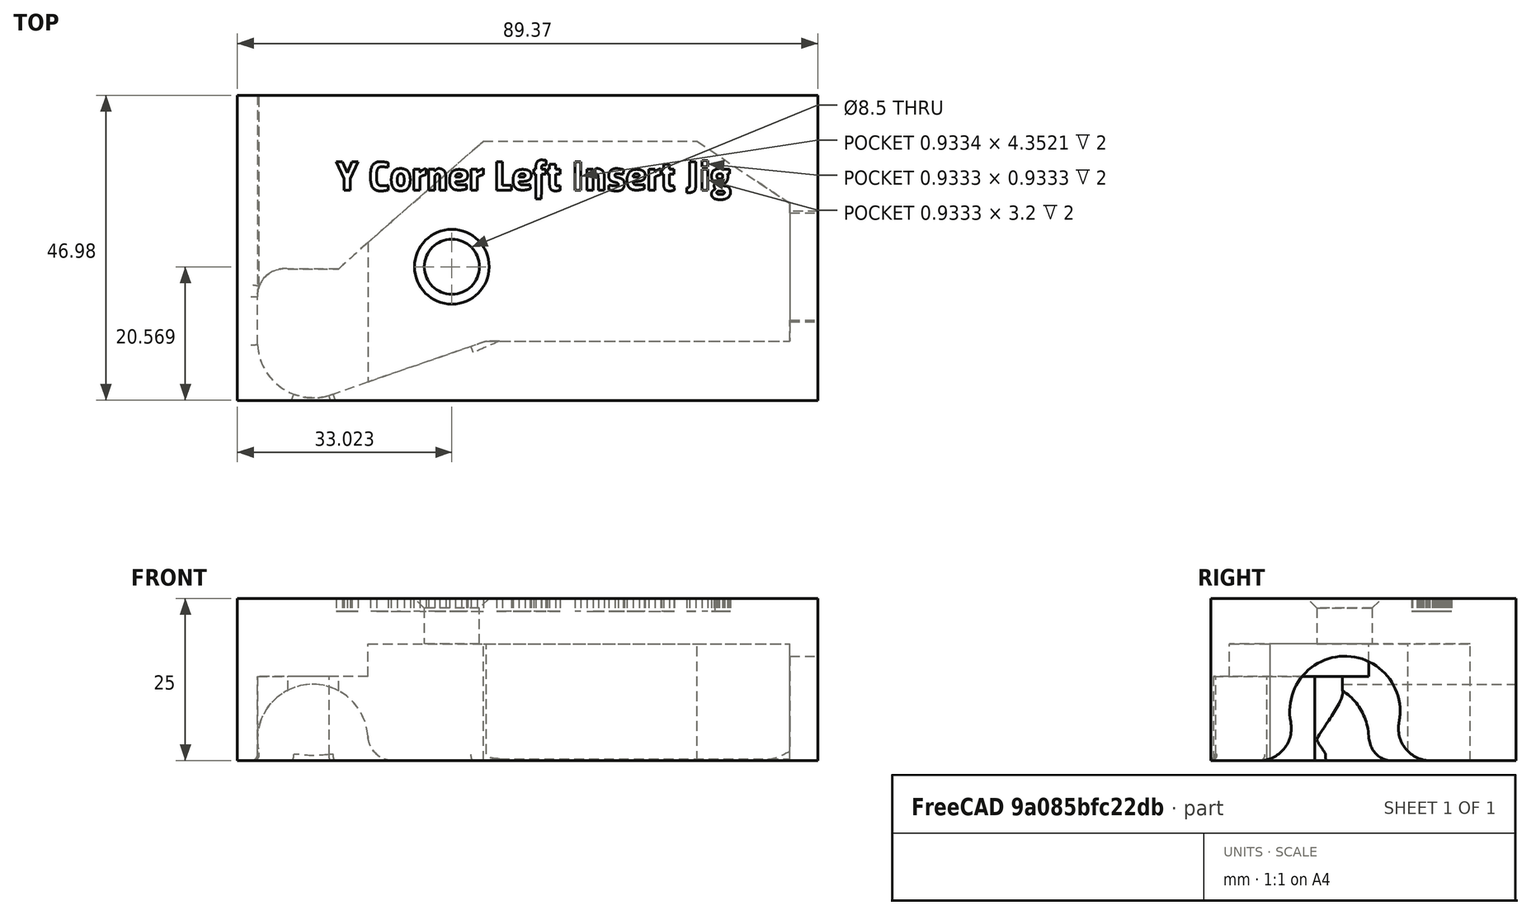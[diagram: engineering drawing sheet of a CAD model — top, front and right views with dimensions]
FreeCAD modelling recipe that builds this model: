
FCSTD DOCUMENT  (FreeCAD 0.17R9537 (Git))
Label: y_corner_left_insert_jig
License: All rights reserved
LicenseURL: http://en.wikipedia.org/wiki/All_rights_reserved
objects: Sketcher::SketchObject×8, PartDesign::Pocket×6, PartDesign::Fillet×3, Mesh::Feature×1, PartDesign::Pad×1, Part::Feature×1, PartDesign::Plane×1, PartDesign::Chamfer×1, Part::Part2DObjectPython×1, PartDesign::Body×1
note: 30 computed .brp shape members not serialized (recipe doc carries the construction recipe); baked Part::Feature solids carry a one-line shape summary decoded from their .brp

FEATURE [Mesh::Feature] y_corner_left_v2_4  label="y_corner_left_v2.4"
  Placement = pos=(-95,-15,-13) rot=(0,0,1;0rad)
FEATURE [Sketcher::SketchObject] Sketch
  MapMode = 5
  Support = -> [XY_Plane]
  sketch-geometry (4):
    g0: LineSegment StartX=-41.2454 StartY=-29.3641 StartZ=0 EndX=48.1248 EndY=-29.3641 EndZ=0
    g1: LineSegment StartX=48.1248 StartY=-29.3641 StartZ=0 EndX=48.1248 EndY=17.6233 EndZ=0
    g2: LineSegment StartX=48.1248 StartY=17.6233 StartZ=0 EndX=-41.2454 EndY=17.6233 EndZ=0
    g3: LineSegment StartX=-41.2454 StartY=17.6233 StartZ=0 EndX=-41.2454 EndY=-29.3641 EndZ=0
  constraints (8):
    c: Coincident(g0,g1)
    c: Coincident(g1,g2)
    c: Coincident(g2,g3)
    c: Coincident(g3,g0)
    c: Horizontal(g0)
    c: Horizontal(g2)
    c: Vertical(g1)
    c: Vertical(g3)
FEATURE [PartDesign::Pad] Pad
  Length = 25
  Length2 = 100
  Profile = -> Sketch
  Type = 0
FEATURE [Part::Feature] y_corner_left_v2_4001
  Placement = pos=(0,0,12) rot=(0,0,1;0rad)
  shape: bbox 81.06 x 37.98 x 18.29 mm, 18592 faces, 0 solids (baked)
FEATURE [Sketcher::SketchObject] Sketch001
  MapMode = 5
  Placement = pos=(0,0,0) rot=(1,0,0;3.14159rad)
  Support = -> [Pad]
  sketch-geometry (7):
    g0: LineSegment StartX=-21.1438 StartY=5.05934 StartZ=0 EndX=-3.38972 EndY=-10.5427 EndZ=0
    g1: LineSegment StartX=-3.38972 StartY=-10.5427 StartZ=0 EndX=29.5098 EndY=-10.5427 EndZ=0
    g2: LineSegment StartX=29.5098 StartY=-10.5427 StartZ=0 EndX=43.8429 EndY=-0.932231 EndZ=0
    g3: LineSegment StartX=43.8429 StartY=-0.932231 StartZ=0 EndX=43.8429 EndY=20.2526 EndZ=0
    g4: LineSegment StartX=-21.1438 StartY=5.05934 StartZ=0 EndX=-21.1438 EndY=26.5193 EndZ=0
    g5: LineSegment StartX=-21.1438 StartY=26.5193 StartZ=0 EndX=-2.94605 EndY=20.2526 EndZ=0
    g6: LineSegment StartX=-2.94605 StartY=20.2526 StartZ=0 EndX=43.8429 EndY=20.2526 EndZ=0
  constraints (11):
    c: Coincident(g1,g0)
    c: Horizontal(g1)
    c: Coincident(g2,g1)
    c: Coincident(g3,g2)
    c: Vertical(g3)
    c: Coincident(g4,g0)
    c: Vertical(g4)
    c: Coincident(g5,g4)
    c: Coincident(g6,g5)
    c: Coincident(g6,g3)
    c: Horizontal(g6)
FEATURE [PartDesign::Pocket] Pocket
  BaseFeature = -> Pad
  Length = 18
  Profile = -> Sketch001
  Type = 0
FEATURE [Sketcher::SketchObject] Sketch002
  ExternalGeometry = -> [Pocket]
  MapMode = 5
  Placement = pos=(0,0,0) rot=(1,0,0;3.14159rad)
  Support = -> [Pocket]
  sketch-geometry (7):
    g0: LineSegment StartX=-21.1438 StartY=5.05934 StartZ=0 EndX=-25.6743 EndY=9.11448 EndZ=0
    g1: LineSegment StartX=-25.6743 StartY=9.11448 StartZ=0 EndX=-33.4497 EndY=9.11448 EndZ=0
    g2: LineSegment StartX=-21.1438 StartY=26.5193 StartZ=0 EndX=-27.1407 EndY=28.6513 EndZ=0
    g3: ArcOfCircle CenterX=-29.5136 CenterY=20.3238 CenterZ=0 NormalX=0 NormalY=0 NormalZ=1 Radius=8.65904 StartAngle=1.2932 EndAngle=3.08945
    g4: LineSegment StartX=-38.1609 StartY=20.7751 StartZ=0 EndX=-38.1609 EndY=13.4153 EndZ=0
    g5: ArcOfCircle CenterX=-33.9785 CenterY=13.266 CenterZ=0 NormalX=0 NormalY=0 NormalZ=1 Radius=4.18506 StartAngle=3.10591 EndAngle=4.83908
    g6: LineSegment StartX=-21.1438 StartY=5.05934 StartZ=0 EndX=-21.1438 EndY=26.5193 EndZ=0
  constraints (11):
    c: Coincident(g0,g-3)
    c: Coincident(g1,g0)
    c: Horizontal(g1)
    c: Coincident(g2,g-3)
    c: Coincident(g3,g2)
    c: Coincident(g4,g3)
    c: Vertical(g4)
    c: Coincident(g1,g5)
    c: Coincident(g4,g5)
    c: Coincident(g6,g0)
    c: Coincident(g6,g2)
FEATURE [PartDesign::Pocket] Pocket001
  BaseFeature = -> Pocket
  Length = 13
  Profile = -> Sketch002
  Type = 0
FEATURE [Sketcher::SketchObject] Sketch003
  MapMode = 5
  Placement = pos=(0,17.6233,0) rot=(0,0.707107,0.707107;3.14159rad)
  Support = -> [Pocket001]
  sketch-geometry (1):
    g0: Circle CenterX=29.6574 CenterY=3.27274 CenterZ=0 NormalX=0 NormalY=0 NormalZ=1 Radius=8.5
  constraints (1):
    c: Radius(g0) = 8.5
FEATURE [PartDesign::Pocket] Pocket002
  BaseFeature = -> Pocket001
  Length = 35
  Profile = -> Sketch003
  Type = 0
FEATURE [Sketcher::SketchObject] Sketch004
  MapMode = 5
  Placement = pos=(48.1248,0,0) rot=(0.57735,0.57735,0.57735;2.0944rad)
  Support = -> [Pocket002]
  sketch-geometry (1):
    g0: Circle CenterX=-8.75085 CenterY=7.61123 CenterZ=0 NormalX=0 NormalY=0 NormalZ=1 Radius=8.5
  constraints (1):
    c: Radius(g0) = 8.5
FEATURE [PartDesign::Pocket] Pocket003
  BaseFeature = -> Pocket002
  Length = 5
  Profile = -> Sketch004
  Type = 0
FEATURE [PartDesign::Fillet] Fillet
  Base = -> Pocket003 [Edge31,Edge23]
  BaseFeature = -> Pocket003
  Radius = 5
FEATURE [PartDesign::Fillet] Fillet001
  Base = -> Fillet [Edge43]
  BaseFeature = -> Fillet
  Radius = 4
FEATURE [PartDesign::Fillet] Fillet002
  Base = -> Fillet001 [Edge32,Edge41,Edge40,Edge38,Edge37,Edge35]
  BaseFeature = -> Fillet001
  Radius = 1
FEATURE [Sketcher::SketchObject] Sketch005
  ExternalGeometry = -> [y_corner_left_v2_4001,Fillet002]
  MapMode = 5
  Placement = pos=(0,-29.3641,0) rot=(1,0,0;1.5708rad)
  Support = -> [Fillet002]
  sketch-geometry (1):
    g0: LineSegment StartX=-26.1602 StartY=0 StartZ=0 EndX=-26.1602 EndY=-0.999892 EndZ=0
  constraints (3):
    c: Coincident(g0,g-4)
    c: PointOnObject(g0,g-3)
    c: Vertical(g0)
FEATURE [Sketcher::SketchObject] Sketch006
  MapMode = 5
  Placement = pos=(0,0,18) rot=(1,0,0;3.14159rad)
  Support = -> [Fillet002]
  sketch-geometry (1):
    g0: Circle CenterX=-8.22724 CenterY=8.79045 CenterZ=0 NormalX=0 NormalY=0 NormalZ=1 Radius=4.25
  constraints (1):
    c: Radius(g0) = 4.25
FEATURE [PartDesign::Pocket] Pocket004
  BaseFeature = -> Fillet002
  Length = 5
  Profile = -> Sketch006
  Type = 1
FEATURE [PartDesign::Plane] DatumPlane
  MapMode = 5
  Placement = pos=(0,0,10) rot=(1,0,0;3.14159rad)
  Support = -> [Pocket004]
  superPlacement = pos=(0,0,-10) rot=(0,0,1;0rad)
FEATURE [Sketcher::SketchObject] Sketch007
  ExternalGeometry = -> [Pocket004]
  MapMode = 5
  Placement = pos=(0,17.6233,0) rot=(0,0.707107,0.707107;3.14159rad)
  Support = -> [Pocket004]
  sketch-geometry (1):
    g0: LineSegment StartX=3.2818 StartY=25 StartZ=0 EndX=3.2818 EndY=9.8977 EndZ=0
  constraints (2):
    c: PointOnObject(g0,g-3)
    c: Vertical(g0)
FEATURE [PartDesign::Chamfer] Chamfer
  Base = -> Pocket004 [Edge37]
  BaseFeature = -> Pocket004
  Size = 1.5
FEATURE [Part::Part2DObjectPython] ShapeString  # Draft 2D object (typed FeaturePython)
  FontFile = <userpath>/Desktop/Titillium-BoldUpright.otf
  Placement = pos=(-26,3,25) rot=(0,0,1;0rad)
  Size = 2.5
  String = Y Corner Left Insert Jig
  Support = -> [Chamfer]
  Tracking = 70
FEATURE [PartDesign::Pocket] Pocket005
  BaseFeature = -> Chamfer
  Length = 2
  Profile = -> ShapeString
  Type = 0
FEATURE [PartDesign::Body] Body
  Model = -> [Sketch,Pad,Sketch001,Pocket,Sketch002,Pocket001,Sketch003,Pocket002,Sketch004,Pocket003,Fillet,Fillet001,Fillet002,Pocket004,DatumPlane,Sketch007,Chamfer,Pocket005]
  Origin = -> BodyOrigin
  Tip = -> Pocket005
